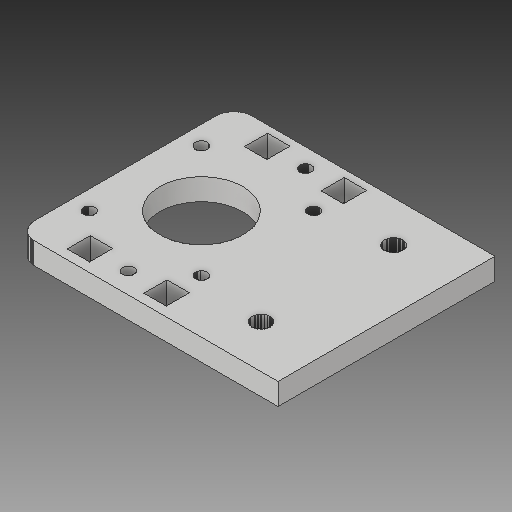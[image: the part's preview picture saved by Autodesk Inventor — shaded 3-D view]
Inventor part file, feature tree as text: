
AUTODESK INVENTOR PART (.ipt)
format: ipt  version: 2018 (Build 220112000, 112)  size: 1,035,776 bytes
history: native  units: mm
features: sketch x4, other x3
ambient origin geometry x8: Origin, YZ Plane, XZ Plane, XY Plane, X Axis, Y Axis, Z Axis, Center Point
bodies: Solid1 (feature_tree)
feature tree (7):
  other  "Y-Motor-Mount Top.ipt"
  other  "Solid1::Y-Motor-Mount Top.ipt"
  other  "TaggingFeature1"
  sketch  "Sketch1"  dims[d0=10.0mm]
  sketch  "Sketch2"
  sketch  "Sketch3"
  sketch  "Sketch4"
